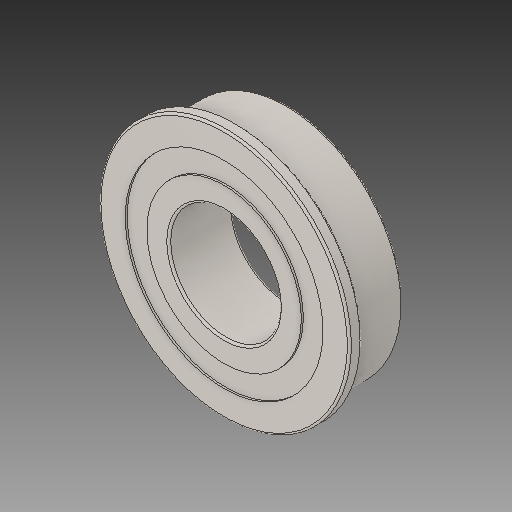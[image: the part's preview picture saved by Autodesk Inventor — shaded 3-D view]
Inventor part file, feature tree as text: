
AUTODESK INVENTOR PART (.ipt)
format: ipt  version: 2017 (Build 210142000, 142)  size: 202,240 bytes
history: native  units: in
note: dims shown in document units (in); Inventor stores cm internally (conversion verified against a paired STEP export)
features: fillet x1
ambient origin geometry x8: Origin, YZ Plane, XZ Plane, XY Plane, X Axis, Y Axis, Z Axis, Center Point
bodies: Solid1 (feature_tree)
feature tree (1):
  fillet  "Fillet1"  [1 undecoded]
note: 1 required parameter value undecoded (feature->parameter linkage not recoverable at this tier; creation-order binding heuristic only, values carry confidence <= 0.55)
